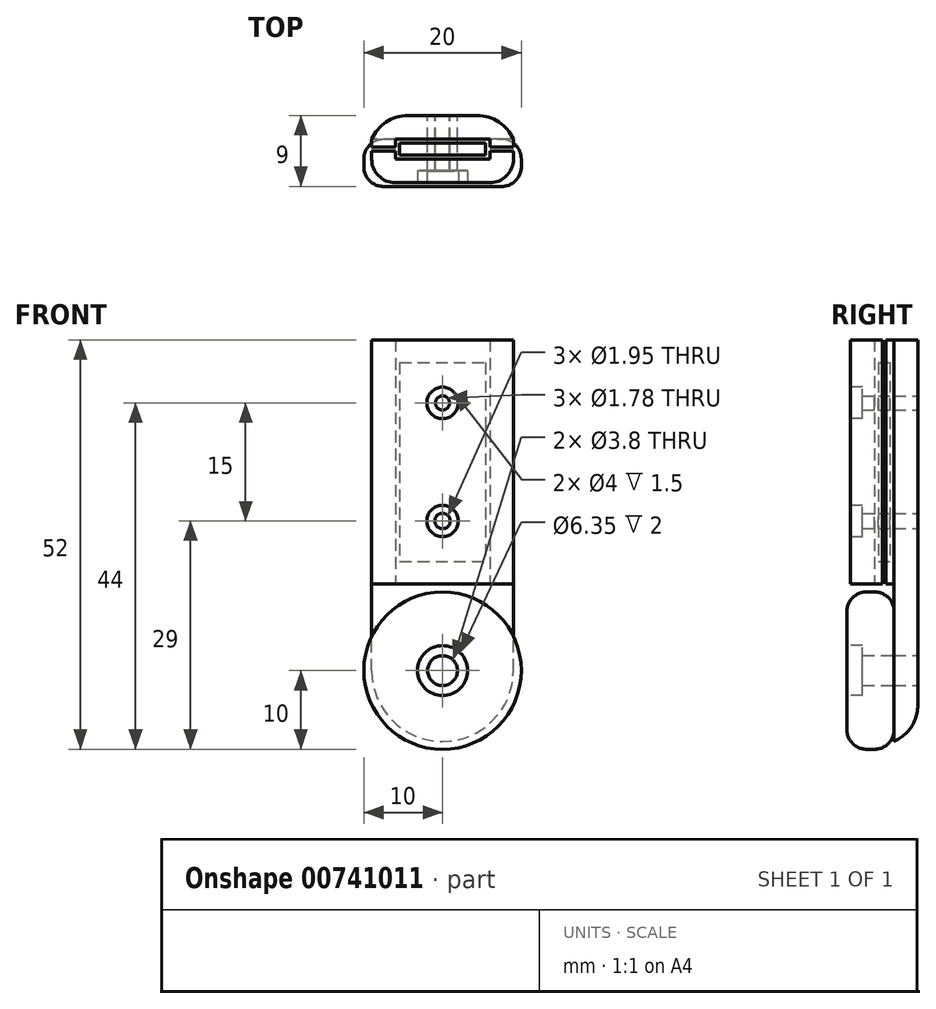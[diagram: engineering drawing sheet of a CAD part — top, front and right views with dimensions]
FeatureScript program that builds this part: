
annotation { "Feature Type Name" : "Feature", "Feature Type Description" : "" }
export const myFeature = defineFeature(function(context is Context, id is Id, definition is map)
    precondition{}
    {
        {
            var Q0;
            Q0=qCreatedBy(makeId("Front.planeOp"),FACE);
            var sketch = newSketch(context, id + "F0", { "sketchPlane" : qUnion([Q0])});
            skLineSegment(sketch, "E0.bottom", {"start": v(-5.46, 12.6) * mm, "end": v(5.46, 12.6) * mm});
            skLineSegment(sketch, "E0.top", {"start": v(-5.46, -12.6) * mm, "end": v(5.46, -12.6) * mm});
            skLineSegment(sketch, "E0.left", {"start": v(-5.46, 12.6) * mm, "end": v(-5.46, -12.6) * mm});
            skLineSegment(sketch, "E0.right", {"start": v(5.46, 12.6) * mm, "end": v(5.46, -12.6) * mm});
            skPoint(sketch, "E0.middle", {"position": v(0, 0) * mm});
            skSolve(sketch);
        }
        {
            var Q0;
            Q0 = qSketchRegion(id + "F0", true);
            extrude(context, id + "F1", {"entities" : qUnion([Q0]), "depth" : 1.52 * mm, "offsetDistance" : 25 * mm});
        }
        {
            var Q0;
            Q0=qCreatedBy(makeId("Top.planeOp"),FACE);
            var sketch = newSketch(context, id + "F2", { "sketchPlane" : qUnion([Q0])});
            skLineSegment(sketch, "E1.bottom", {"start": v(6, 0.5) * mm, "end": v(-6, 0.5) * mm});
            skLineSegment(sketch, "E1.top", {"start": v(6, -2.02) * mm, "end": v(-6, -2.02) * mm});
            skLineSegment(sketch, "E1.left", {"start": v(6, 0.5) * mm, "end": v(6, -2.02) * mm});
            skLineSegment(sketch, "E1.right", {"start": v(-6, 0.5) * mm, "end": v(-6, -2.02) * mm});
            skPoint(sketch, "E1.middle", {"position": v(0, -0.76) * mm});
            skLineSegment(sketch, "E2", {"start": v(6, -0.76) * mm, "end": v(-6, -0.76) * mm, "construction": true});
            skLineSegment(sketch, "E3.0", {"start": v(9, 3.5) * mm, "end": v(9, -2.02) * mm});
            skLineSegment(sketch, "E3.1", {"start": v(9, 3.5) * mm, "end": v(-9, 3.5) * mm});
            skLineSegment(sketch, "E3.2", {"start": v(-9, 3.5) * mm, "end": v(-9, -2.02) * mm});
            skLineSegment(sketch, "E3.3", {"start": v(6, -5.02) * mm, "end": v(-6, -5.02) * mm});
            skLineSegment(sketch, "E4", {"start": v(-6, -1.01) * mm, "end": v(-9, -1.01) * mm});
            skLineSegment(sketch, "E5", {"start": v(6, -1.01) * mm, "end": v(9, -1.01) * mm});
            skLineSegment(sketch, "E6.MirrorCS", {"start": v(-6, -0.51) * mm, "end": v(-9, -0.51) * mm});
            skLineSegment(sketch, "E7.MirrorCS", {"start": v(6, -0.51) * mm, "end": v(9, -0.51) * mm});
            skPoint(sketch, "E8.visualSharp", {"position": v(-9, -5.02) * mm});
            skArc(sketch, "E8.filletArc", {"start": v(-9, -2.02) * mm, "mid": v(-8.12, -4.15) * mm, "end": v(-6, -5.02) * mm});
            skPoint(sketch, "E9.visualSharp", {"position": v(9, -5.02) * mm});
            skArc(sketch, "E9.filletArc", {"start": v(6, -5.02) * mm, "mid": v(8.12, -4.15) * mm, "end": v(9, -2.02) * mm});
            skSolve(sketch);
        }
        {
            var Q0;
            {var subQ4=sQuery(id+"F2.wireOp",EDGE,"E1.bottom");Q0=makeQuery(id+"F2.imprint","IMPRINT",FACE,{"disambiguationData":[TD([[makeQuery(id+"F2.imprint","IMPRINT",EDGE,{"derivedFrom":subQ4}),-1.0]])]});}
            var Q1;
            {var subQ4=sQuery(id+"F2.wireOp",EDGE,"E1.top");Q1=makeQuery(id+"F2.imprint","IMPRINT",FACE,{"disambiguationData":[TD([[makeQuery(id+"F2.imprint","IMPRINT",EDGE,{"derivedFrom":subQ4}),1.0]])]});}
            extrude(context, id + "F3", {"entities" : qUnion([Q0, Q1]), "endBound" : BoundingType.SYMMETRIC, "depth" : 31 * mm, "offsetDistance" : 25 * mm});
        }
        {
            var Q0;
            Q0=makeQuery(id+"F1.opExtrude","CAP_FACE",FACE,{"disambiguationData":[OSD([sQuery(id+"F0.wireOp",EDGE,"E0.bottom"),sQuery(id+"F0.wireOp",EDGE,"E0.top"),sQuery(id+"F0.wireOp",EDGE,"E0.left"),sQuery(id+"F0.wireOp",EDGE,"E0.right")])],"isStart":true});
            var sketch = newSketch(context, id + "F4", { "sketchPlane" : qUnion([Q0])});
            skCircle(sketch, "E10", {"center": v(0, 7.5) * mm, "radius": 0.89 * mm});
            skCircle(sketch, "E11", {"center": v(0, -7.5) * mm, "radius": 0.97 * mm});
            skSolve(sketch);
        }
        {
            var Q0;
            Q0 = qSketchRegion(id + "F4", true);
            extrude(context, id + "F5", {"entities" : qUnion([Q0]), "operationType" : NewBodyOperationType.REMOVE, "endBound" : BoundingType.SYMMETRIC, "oppositeDirection" : true, "depth" : 25 * mm, "offsetDistance" : 25 * mm});
        }
        {
            var Q0;
            Q0=makeQuery(id+"F3.opExtrude","CAP_FACE",FACE,{"disambiguationData":[OSD([sQuery(id+"F2.wireOp",EDGE,"E1.bottom"),sQuery(id+"F2.wireOp",EDGE,"E1.left"),sQuery(id+"F2.wireOp",EDGE,"E1.right"),sQuery(id+"F2.wireOp",EDGE,"E3.0"),sQuery(id+"F2.wireOp",EDGE,"E3.1"),sQuery(id+"F2.wireOp",EDGE,"E3.2"),sQuery(id+"F2.wireOp",EDGE,"E6.MirrorCS"),sQuery(id+"F2.wireOp",EDGE,"E7.MirrorCS")])],"isStart":true});
            var sketch = newSketch(context, id + "F6", { "sketchPlane" : qUnion([Q0])});
            skLineSegment(sketch, "E12.bottom", {"start": v(9, -3.5) * mm, "end": v(-9, -3.5) * mm});
            skLineSegment(sketch, "E12.top", {"start": v(9, -0.5) * mm, "end": v(-9, -0.5) * mm});
            skLineSegment(sketch, "E12.left", {"start": v(9, -3.5) * mm, "end": v(9, -0.5) * mm});
            skLineSegment(sketch, "E12.right", {"start": v(-9, -3.5) * mm, "end": v(-9, -0.5) * mm});
            skSolve(sketch);
        }
        {
            var Q0;
            Q0 = qSketchRegion(id + "F6", true);
            extrude(context, id + "F7", {"entities" : qUnion([Q0]), "operationType" : NewBodyOperationType.ADD, "depth" : 20 * mm, "offsetDistance" : 25 * mm});
        }
        {
            var Q0;
            Q0=makeQuery(id+"F7.boolean.opBoolean","MERGE",FACE,{"derivedFrom":[makeQuery(id+"F3.opExtrude","SWEPT_FACE",FACE,{"disambiguationData":[OSD([sQuery(id+"F2.wireOp",EDGE,"E3.1")])]}),makeQuery(id+"F7.opExtrude","SWEPT_FACE",FACE,{"disambiguationData":[OSD([sQuery(id+"F6.wireOp",EDGE,"E12.bottom")])]})]});
            var sketch = newSketch(context, id + "F8", { "sketchPlane" : qUnion([Q0])});
            skSolve(sketch);
        }
        {
            var Q0;
            Q0=makeQuery(id+"F7.opExtrude","CAP_EDGE",EDGE,{"disambiguationData":[OSD([sQuery(id+"F6.wireOp",EDGE,"E12.right")])],"isStart":false});
            var Q1;
            Q1=makeQuery(id+"F7.opExtrude","CAP_EDGE",EDGE,{"disambiguationData":[OSD([sQuery(id+"F6.wireOp",EDGE,"E12.left")])],"isStart":false});
            fillet(context, id + "F9", {"entities" : qUnion([Q0, Q1]), "radius" : 9 * mm, "tangentPropagation" : true, "allowEdgeOverflow" : false});
        }
        {
            var Q0;
            Q0=makeQuery(id+"F7.boolean.opBoolean","MERGE",FACE,{"derivedFrom":[makeQuery(id+"F3.opExtrude","SWEPT_FACE",FACE,{"disambiguationData":[OSD([sQuery(id+"F2.wireOp",EDGE,"E1.bottom")])]}),makeQuery(id+"F7.opExtrude","SWEPT_FACE",FACE,{"disambiguationData":[OSD([sQuery(id+"F6.wireOp",EDGE,"E12.top")])]})]});
            var sketch = newSketch(context, id + "F10", { "sketchPlane" : qUnion([Q0])});
            skCircle(sketch, "E13", {"center": v(0, -26.5) * mm, "radius": 1.9 * mm});
            skCircle(sketch, "E14", {"center": v(0, -26.5) * mm, "radius": 10 * mm});
            skCircle(sketch, "E15", {"center": v(0, -26.5) * mm, "radius": 3.17 * mm});
            skSolve(sketch);
        }
        {
            var Q0;
            Q0 = qSketchRegion(id + "F10", true);
            var Q1;
            Q1=makeQuery(id+"F10.imprint","IMPRINT",FACE,{"disambiguationData":[TD([[makeQuery(id+"F10.imprint","IMPRINT",EDGE,{"derivedFrom":sQuery(id+"F10.wireOp",EDGE,"E13")}),-1.0]])]});
            extrude(context, id + "F11", {"entities" : qUnion([Q0, Q1]), "depth" : 6 * mm, "offsetDistance" : 25 * mm});
        }
        {
            var Q0;
            Q0=makeQuery(id+"F11.opExtrude","CAP_EDGE",EDGE,{"disambiguationData":[OSD([sQuery(id+"F10.wireOp",EDGE,"E14")])],"isStart":false});
            var Q1;
            Q1=makeQuery(id+"F11.opExtrude","CAP_EDGE",EDGE,{"disambiguationData":[OSD([sQuery(id+"F10.wireOp",EDGE,"E14")])],"isStart":true});
            fillet(context, id + "F12", {"entities" : qUnion([Q0, Q1]), "radius" : 2.5 * mm, "tangentPropagation" : true, "allowEdgeOverflow" : false});
        }
        {
            var Q0;
            Q0=makeQuery(id+"F7.boolean.opBoolean","MERGE",EDGE,{"derivedFrom":[makeQuery(id+"F3.opExtrude","SWEPT_EDGE",EDGE,{"disambiguationData":[OSD([sQuery(id+"F2.wireOp",EDGE,"E3.1"),sQuery(id+"F2.wireOp",EDGE,"E3.2")])]}),makeQuery(id+"F7.opExtrude","SWEPT_EDGE",EDGE,{"disambiguationData":[OSD([sQuery(id+"F6.wireOp",EDGE,"E12.bottom"),sQuery(id+"F6.wireOp",EDGE,"E12.right")])]})]});
            fillet(context, id + "F13", {"entities" : qUnion([Q0]), "radius" : 5 * mm, "tangentPropagation" : true, "allowEdgeOverflow" : false});
        }
        {
            var Q0;
            {var subQ1=sQuery(id+"F2.wireOp",EDGE,"E3.1");Q0=makeQuery(id+"F8.imprint","IMPRINT",FACE,{"disambiguationData":[TD([[makeQuery(id+"F8.imprint","IMPRINT",EDGE,{"derivedFrom":makeQuery(id+"F3.opExtrude","CAP_EDGE",EDGE,{"disambiguationData":[OSD([subQ1])],"isStart":false})}),-1.0]])]});}
            var sketch = newSketch(context, id + "F14", { "sketchPlane" : qUnion([Q0])});
            skCircle(sketch, "E16.0", {"center": v(0, -26.5) * mm, "radius": 1.9 * mm});
            skSolve(sketch);
        }
        {
            var Q0;
            Q0 = qSketchRegion(id + "F14", true);
            extrude(context, id + "F15", {"entities" : qUnion([Q0]), "operationType" : NewBodyOperationType.REMOVE, "oppositeDirection" : true, "depth" : 25 * mm, "offsetDistance" : 25 * mm});
        }
        {
            var Q0;
            Q0=makeQuery(id+"F3.opExtrude","SWEPT_FACE",FACE,{"disambiguationData":[OSD([sQuery(id+"F2.wireOp",EDGE,"E3.3")])]});
            var sketch = newSketch(context, id + "F16", { "sketchPlane" : qUnion([Q0])});
            skCircle(sketch, "E17", {"center": v(0, 7.5) * mm, "radius": 2 * mm});
            skCircle(sketch, "E18", {"center": v(0, -7.5) * mm, "radius": 2 * mm});
            skSolve(sketch);
        }
        {
            var Q0;
            Q0 = qSketchRegion(id + "F16", true);
            extrude(context, id + "F17", {"entities" : qUnion([Q0]), "operationType" : NewBodyOperationType.REMOVE, "oppositeDirection" : true, "depth" : 1.5 * mm, "offsetDistance" : 25 * mm});
        }
        {
            var Q0;
            Q0=makeQuery(id+"F11.opExtrude","CAP_FACE",FACE,{"disambiguationData":[OSD([sQuery(id+"F10.wireOp",EDGE,"E13"),sQuery(id+"F10.wireOp",EDGE,"E14")])],"isStart":false});
            var sketch = newSketch(context, id + "F18", { "sketchPlane" : qUnion([Q0])});
            skCircle(sketch, "E19", {"center": v(0, -26.5) * mm, "radius": 3.17 * mm});
            skSolve(sketch);
        }
        {
            var Q0;
            Q0 = qSketchRegion(id + "F18", true);
            extrude(context, id + "F19", {"entities" : qUnion([Q0]), "operationType" : NewBodyOperationType.REMOVE, "oppositeDirection" : true, "depth" : 2 * mm, "offsetDistance" : 25 * mm});
        }
    });
